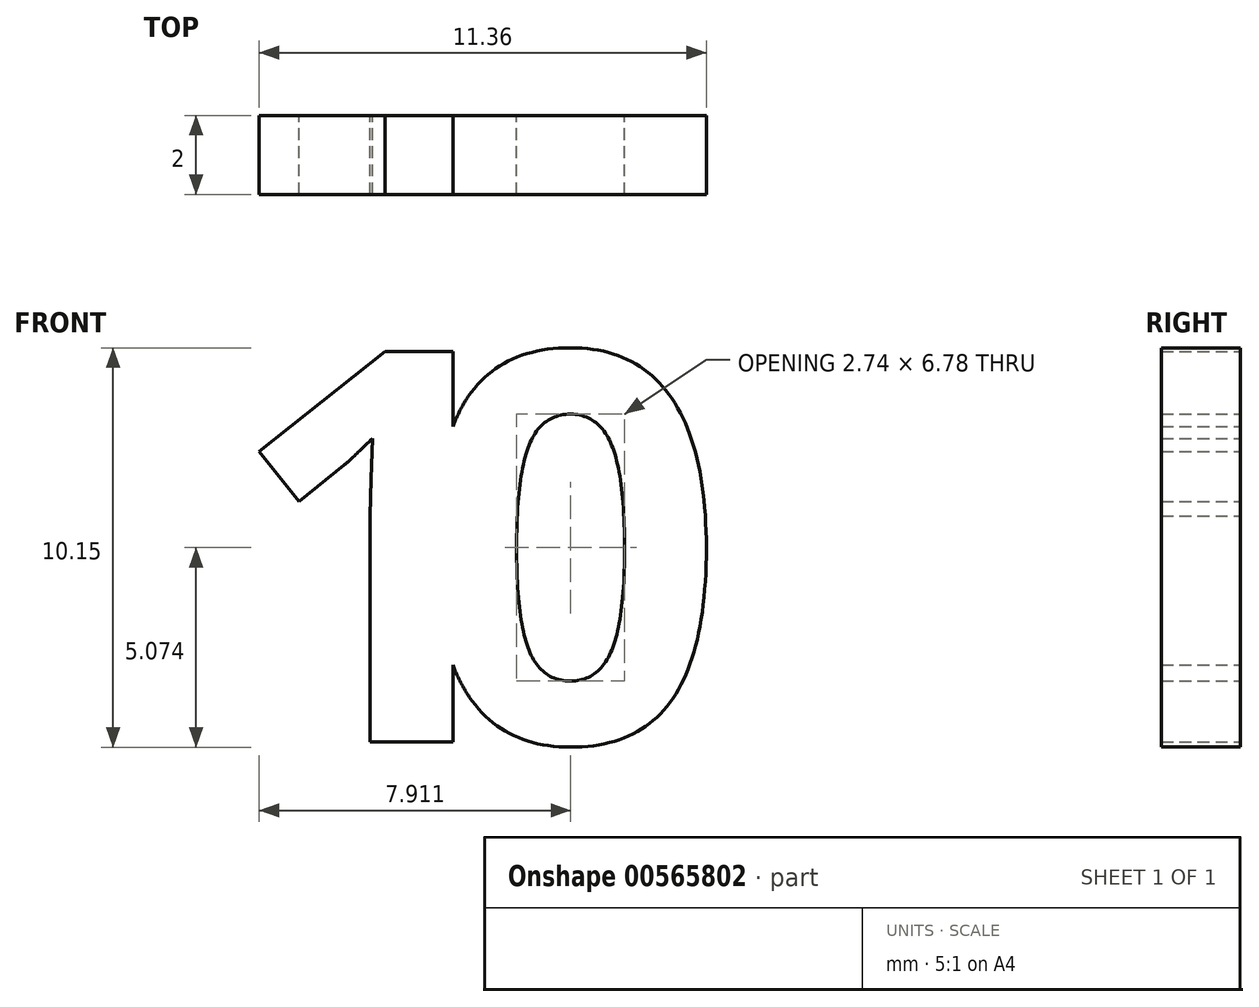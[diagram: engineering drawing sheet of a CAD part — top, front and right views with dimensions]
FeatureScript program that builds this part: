
annotation { "Feature Type Name" : "Feature", "Feature Type Description" : "" }
export const myFeature = defineFeature(function(context is Context, id is Id, definition is map)
    precondition{}
    {
        {
            var Q0;
            Q0=qCreatedBy(makeId("Front.planeOp"),FACE);
            var sketch = newSketch(context, id + "F0", { "sketchPlane" : qUnion([Q0])});
            skLineSegment(sketch, "E0", {"start": v(0, 0) * mm, "end": v(0, 10) * mm});
            skText(sketch, "E1", { "text": "1", "fontName": "OpenSans-Bold.ttf"});
            const initialGuessF0  = {"E1": [0, 0, 1, 0, 0.01]};
            skSetInitialGuess(sketch, initialGuessF0);
            skSolve(sketch);
        }
        {
            var Q0;
            Q0=makeQuery(id+"F0.imprint","IMPRINT",FACE,{"disambiguationData":[TD([[makeQuery(id+"F0.imprint","IMPRINT",EDGE,{"derivedFrom":sQuery(id+"F0.wireOp",EDGE,"E1.sketch_text.stroke-0")}),-1.0]])]});
            extrude(context, id + "F1", {"entities" : qUnion([Q0]), "depth" : 2 * mm, "offsetDistance" : 25 * mm});
        }
        {
            var Q0;
            Q0=qCreatedBy(makeId("Front.planeOp"),FACE);
            var sketch = newSketch(context, id + "F2", { "sketchPlane" : qUnion([Q0])});
            skText(sketch, "E2", { "text": "0", "fontName": "OpenSans-Bold.ttf"});
            const initialGuessF2  = {"E2": [0.00479, 0, 1, 0, 0.00994]};
            skSetInitialGuess(sketch, initialGuessF2);
            skSolve(sketch);
        }
        {
            var Q0;
            Q0 = qSketchRegion(id + "F2", true);
            extrude(context, id + "F3", {"entities" : qUnion([Q0]), "operationType" : NewBodyOperationType.ADD, "depth" : 2 * mm, "offsetDistance" : 25 * mm});
        }
    });
